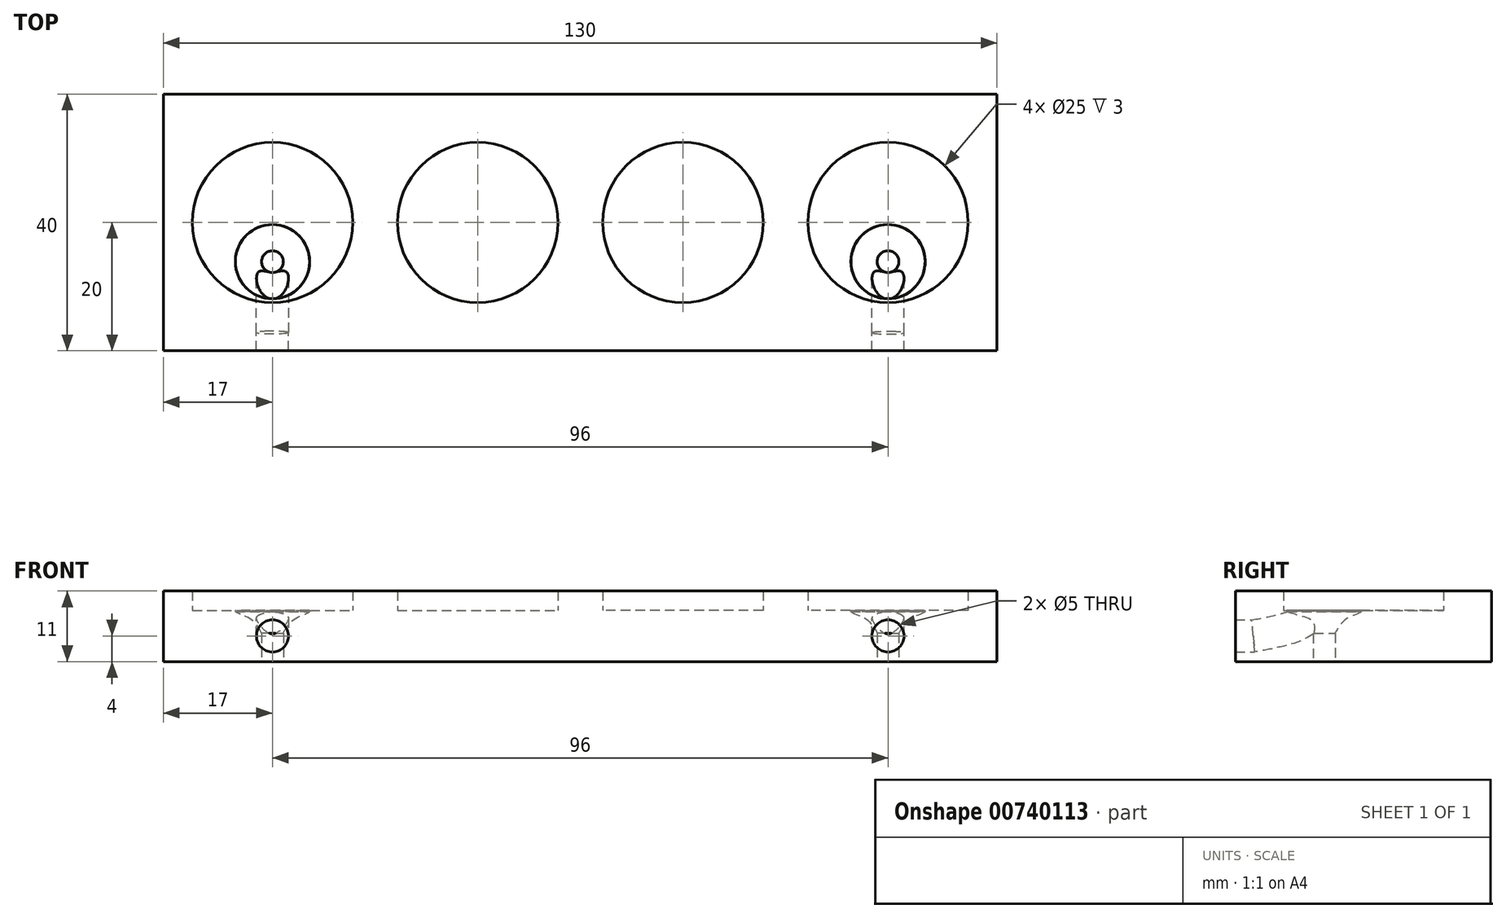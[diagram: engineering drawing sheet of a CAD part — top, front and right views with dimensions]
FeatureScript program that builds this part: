
annotation { "Feature Type Name" : "Feature", "Feature Type Description" : "" }
export const myFeature = defineFeature(function(context is Context, id is Id, definition is map)
    precondition{}
    {
        {
            var Q0;
            Q0=qCreatedBy(makeId("Top.planeOp"),FACE);
            var sketch = newSketch(context, id + "F0", { "sketchPlane" : qUnion([Q0])});
            skLineSegment(sketch, "E0.bottom", {"start": v(65, 20) * mm, "end": v(-65, 20) * mm});
            skLineSegment(sketch, "E0.top", {"start": v(65, -20) * mm, "end": v(-65, -20) * mm});
            skLineSegment(sketch, "E0.left", {"start": v(65, 20) * mm, "end": v(65, -20) * mm});
            skLineSegment(sketch, "E0.right", {"start": v(-65, 20) * mm, "end": v(-65, -20) * mm});
            skPoint(sketch, "E0.middle", {"position": v(0, 0) * mm});
            skCircle(sketch, "E1", {"center": v(-16, 0) * mm, "radius": 12.5 * mm});
            skCircle(sketch, "E2", {"center": v(-48, 0) * mm, "radius": 12.5 * mm});
            skCircle(sketch, "E3.MirrorC", {"center": v(16, 0) * mm, "radius": 12.5 * mm});
            skCircle(sketch, "E4.MirrorC", {"center": v(48, 0) * mm, "radius": 12.5 * mm});
            skSolve(sketch);
        }
        {
            var Q0;
            Q0=makeQuery(id+"F0.imprint","IMPRINT",FACE,{"disambiguationData":[TD([[makeQuery(id+"F0.imprint","IMPRINT",EDGE,{"derivedFrom":sQuery(id+"F0.wireOp",EDGE,"E0.bottom")}),1.0]])]});
            extrude(context, id + "F1", {"entities" : qUnion([Q0]), "depth" : 3 * mm, "offsetDistance" : 25.4 * mm});
        }
        {
            var Q0;
            Q0=qCreatedBy(makeId("Top.planeOp"),FACE);
            var sketch = newSketch(context, id + "F2", { "sketchPlane" : qUnion([Q0])});
            skLineSegment(sketch, "E5.bottom", {"start": v(65, -20) * mm, "end": v(-65, -20) * mm});
            skLineSegment(sketch, "E5.top", {"start": v(65, 20) * mm, "end": v(-65, 20) * mm});
            skLineSegment(sketch, "E5.left", {"start": v(65, -20) * mm, "end": v(65, 20) * mm});
            skLineSegment(sketch, "E5.right", {"start": v(-65, -20) * mm, "end": v(-65, 20) * mm});
            skPoint(sketch, "E5.middle", {"position": v(0, 0) * mm});
            skSolve(sketch);
        }
        {
            var Q0;
            Q0 = qSketchRegion(id + "F2", true);
            extrude(context, id + "F3", {"entities" : qUnion([Q0]), "operationType" : NewBodyOperationType.ADD, "oppositeDirection" : true, "depth" : 8 * mm, "offsetDistance" : 25.4 * mm});
        }
        {
            var Q0;
            Q0=qCreatedBy(makeId("Front.planeOp"),FACE);
            var sketch = newSketch(context, id + "F4", { "sketchPlane" : qUnion([Q0])});
            skLineSegment(sketch, "E6", {"start": v(60.5, 0) * mm, "end": v(35.5, 0) * mm});
            skSolve(sketch);
        }
        {
            var Q0;
            Q0=qCreatedBy(makeId("Right.planeOp"),FACE);
            var sketch = newSketch(context, id + "F5", { "sketchPlane" : qUnion([Q0])});
            skLineSegment(sketch, "E7.bottom", {"start": v(35.81, -28.05) * mm, "end": v(-42.11, -28.05) * mm});
            skLineSegment(sketch, "E7.top", {"start": v(35.81, 17.28) * mm, "end": v(-42.11, 17.28) * mm});
            skLineSegment(sketch, "E7.left", {"start": v(35.81, -28.05) * mm, "end": v(35.81, 17.28) * mm});
            skLineSegment(sketch, "E7.right", {"start": v(-42.11, -28.05) * mm, "end": v(-42.11, 17.28) * mm});
            skSolve(sketch);
        }
        {
            var Q0;
            Q0=makeQuery(id+"F5.imprint","IMPRINT",FACE,{"disambiguationData":[TD([[makeQuery(id+"F5.imprint","IMPRINT",EDGE,{"derivedFrom":sQuery(id+"F5.wireOp",EDGE,"E7.bottom")}),-1.0]])]});
            extrude(context, id + "F6", {"entities" : qUnion([Q0]), "operationType" : NewBodyOperationType.REMOVE, "oppositeDirection" : true, "depth" : 83 * mm, "offsetDistance" : 25 * mm});
        }
        {
            var Q0;
            Q0=sQuery(id+"F4.wireOp",EDGE,"E6");
            cPoint(context, id + "F7", {"entities" : qUnion([Q0]), "parameter" : 0.5});
        }
        {
            var Q0;
            Q0 = qCreatedBy(id + "F7" ,VERTEX);
            var Q1;
            Q1=qCreatedBy(makeId("Right.planeOp"),FACE);
            cPlane(context, id + "F8", {"entities" : qUnion([Q0, Q1]), "cplaneType" : CPlaneType.PLANE_POINT, "offset" : 25 * mm, "width" : 150 * mm, "height" : 150 * mm});
        }
        {
            var Q0;
            Q0=qCreatedBy(id+"F8.planeOp",FACE);
            var sketch = newSketch(context, id + "F9", { "sketchPlane" : qUnion([Q0])});
            skLineSegment(sketch, "E8", {"start": v(0, 0) * mm, "end": v(-20, 0) * mm, "construction": true});
            skLineSegment(sketch, "E9", {"start": v(0, 2.56) * mm, "end": v(-13, 2.56) * mm, "construction": true});
            skLineSegment(sketch, "E10", {"start": v(0, 0) * mm, "end": v(0, -8) * mm, "construction": true});
            skLineSegment(sketch, "E11", {"start": v(0, -4) * mm, "end": v(-14.4, -4) * mm, "construction": true});
            skLineSegment(sketch, "E12", {"start": v(-20, -4) * mm, "end": v(-17.2, -4) * mm});
            skLineSegment(sketch, "E13", {"start": v(-6.5, 2.56) * mm, "end": v(-6.5, -9.38) * mm, "construction": true});
            skLineSegment(sketch, "E14.trimOffspring", {"start": v(-17.2, -4) * mm, "end": v(-28.78, -4) * mm, "construction": true});
            skFitSpline(sketch, "E15", {"points": [v(-6.5, 2.56) * mm, v(-6.72, 1.46) * mm, v(-7.26, 0.3) * mm, v(-8.77, -1.28) * mm, v(-11.18, -2.61) * mm, v(-17.2, -4) * mm], "startDerivative": vector(-1.35, -8.2) * mm, "endDerivative": vector(-21.14, -3.95) * mm});
            skSolve(sketch);
        }
        {
            var Q0;
            Q0=makeQuery(id+"F3.boolean.opBoolean","MERGE",FACE,{"derivedFrom":[makeQuery(id+"F1.opExtrude","SWEPT_FACE",FACE,{"disambiguationData":[OSD([sQuery(id+"F0.wireOp",EDGE,"E0.top")])]}),makeQuery(id+"F3.opExtrude","SWEPT_FACE",FACE,{"disambiguationData":[OSD([sQuery(id+"F2.wireOp",EDGE,"E5.bottom")])]})]});
            var sketch = newSketch(context, id + "F10", { "sketchPlane" : qUnion([Q0])});
            skPoint(sketch, "E16.0", {"position": v(48, -4) * mm});
            skCircle(sketch, "E17", {"center": v(48, -4) * mm, "radius": 2.5 * mm});
            skSolve(sketch);
        }
        {
            var Q0;
            Q0=makeQuery(id+"F10.imprint","IMPRINT",FACE,{"disambiguationData":[TD([[makeQuery(id+"F10.imprint","IMPRINT",EDGE,{"derivedFrom":sQuery(id+"F10.wireOp",EDGE,"E17")}),1.0]])]});
            var Q1;
            Q1=sQuery(id+"F9.wireOp",EDGE,"E12");
            var Q2;
            Q2=sQuery(id+"F9.wireOp",EDGE,"E15");
            sweep(context, id + "F11", {"operationType" : NewBodyOperationType.REMOVE, "profiles" : qUnion([Q0]), "path" : qUnion([Q1, Q2])});
        }
        {
            var Q0;
            Q0=makeQuery(id+"F3.boolean.opBoolean","SPLIT",FACE,{"disambiguationData":[TD([makeQuery(id+"F1.opExtrude","SWEPT_FACE",FACE,{"disambiguationData":[OSD([sQuery(id+"F0.wireOp",EDGE,"E4.MirrorC")])]})])],"derivedFrom":makeQuery(id+"F3.opExtrude","CAP_FACE",FACE,{"disambiguationData":[OSD([sQuery(id+"F2.wireOp",EDGE,"E5.bottom"),sQuery(id+"F2.wireOp",EDGE,"E5.top"),sQuery(id+"F2.wireOp",EDGE,"E5.left"),sQuery(id+"F2.wireOp",EDGE,"E5.right")])],"isStart":true})});
            var sketch = newSketch(context, id + "F12", { "sketchPlane" : qUnion([Q0])});
            skLineSegment(sketch, "E18", {"start": v(48, -12.5) * mm, "end": v(48, 13) * mm, "construction": true});
            skLineSegment(sketch, "E19", {"start": v(48, 0.25) * mm, "end": v(48, -12.5) * mm, "construction": true});
            skSolve(sketch);
        }
        {
            var Q0;
            Q0=qCreatedBy(id+"F8.planeOp",FACE);
            var sketch = newSketch(context, id + "F13", { "sketchPlane" : qUnion([Q0])});
            skPoint(sketch, "E20.0", {"position": v(-6.12, 0) * mm});
            skFitSpline(sketch, "E21.0", {"points": [v(-11.4, 0) * mm, v(-9.13, 0) * mm, v(-6.86, 0) * mm, v(-4.6, 0) * mm]});
            skLineSegment(sketch, "E22", {"start": v(-6.32, -9.5) * mm, "end": v(-7.82, -9.5) * mm});
            skFitSpline(sketch, "E23", {"points": [v(-11.92, 0) * mm, v(-11.92, -0.17) * mm, v(-11.92, -0.23) * mm, v(-10.57, -0.84) * mm, v(-9.28, -1.55) * mm, v(-8.24, -2.83) * mm, v(-7.82, -3.56) * mm, v(-7.82, -3.6) * mm], "startDerivative": vector(0.18, -2.66) * mm, "endDerivative": vector(-0.17, -1.01) * mm});
            skLineSegment(sketch, "E24", {"start": v(-7.82, -3.58) * mm, "end": v(-7.82, -9.5) * mm});
            skLineSegment(sketch, "E25", {"start": v(-11.92, 0) * mm, "end": v(-6.12, 0) * mm});
            skLineSegment(sketch, "E26", {"start": v(-11.92, 0) * mm, "end": v(-11.91, -0.23) * mm});
            skFitSpline(sketch, "E27", {"points": [v(-7.82, -3.58) * mm, v(-8.03, -2.35) * mm, v(-9.14, -1.15) * mm, v(-11.91, -0.23) * mm], "startDerivative": vector(-0.23, 4.62) * mm, "endDerivative": vector(-7.37, 1.76) * mm});
            skLineSegment(sketch, "E28", {"start": v(-6.12, 0) * mm, "end": v(-6.12, -9.5) * mm});
            skLineSegment(sketch, "E29", {"start": v(-6.12, -9.5) * mm, "end": v(-6.32, -9.5) * mm});
            skSolve(sketch);
        }
        {
            var Q0;
            Q0 = qSketchRegion(id + "F13", true);
            var Q1;
            Q1=sQuery(id+"F13.wireOp",EDGE,"E28");
            revolve(context, id + "F14", {"operationType" : NewBodyOperationType.REMOVE, "surfaceOperationType" : NewSurfaceOperationType.NEW, "entities" : qUnion([Q0]), "axis" : qUnion([Q1]), "revolveType" : RevolveType.FULL, "oppositeDirection" : true});
        }
        {
            var Q0;
            Q0=qCreatedBy(makeId("Top.planeOp"),FACE);
            var sketch = newSketch(context, id + "F15", { "sketchPlane" : qUnion([Q0])});
            skPoint(sketch, "E30.0", {"position": v(48, 0.25) * mm});
            skLineSegment(sketch, "E31.0.0", {"start": v(0, 20) * mm, "end": v(0, -20) * mm});
            skLineSegment(sketch, "E31.0.1", {"start": v(0, -20) * mm, "end": v(65, -20) * mm});
            skLineSegment(sketch, "E31.0.2", {"start": v(65, -20) * mm, "end": v(65, 20) * mm});
            skLineSegment(sketch, "E31.0.3", {"start": v(65, 20) * mm, "end": v(0, 20) * mm});
            skCircle(sketch, "E32", {"center": v(16, 0) * mm, "radius": 12.5 * mm});
            skLineSegment(sketch, "E33", {"start": v(48, 0.25) * mm, "end": v(16, 0) * mm, "construction": true});
            skCircle(sketch, "E34", {"center": v(16, 0) * mm, "radius": 12.5 * mm, "construction": true});
            skCircle(sketch, "E35", {"center": v(48, 0) * mm, "radius": 12.5 * mm, "construction": true});
            skFitSpline(sketch, "E36", {"points": [v(50.3, -7.48) * mm, v(50.3, -7.28) * mm, v(50.28, -6.99) * mm, v(50.2, -6.6) * mm, v(50.09, -6.22) * mm, v(49.88, -5.78) * mm, v(49.57, -5.38) * mm, v(49.28, -5.12) * mm, v(49.04, -4.94) * mm, v(48.77, -4.8) * mm, v(48.4, -4.66) * mm, v(48, -4.59) * mm, v(47.62, -4.6) * mm, v(47.22, -4.65) * mm, v(46.85, -4.78) * mm, v(46.5, -4.98) * mm, v(46.19, -5.22) * mm, v(45.91, -5.52) * mm, v(45.7, -5.85) * mm, v(45.52, -6.2) * mm, v(45.37, -6.68) * mm, v(45.3, -7.27) * mm, v(45.3, -7.86) * mm, v(45.36, -8.25) * mm, v(45.4, -8.45) * mm, v(45.46, -8.69) * mm, v(45.6, -9.16) * mm, v(45.85, -9.72) * mm, v(46.11, -10.14) * mm, v(46.33, -10.44) * mm, v(46.57, -10.72) * mm, v(46.74, -10.9) * mm, v(46.84, -10.98) * mm, v(46.98, -11.1) * mm, v(47.2, -11.25) * mm, v(47.53, -11.37) * mm, v(47.8, -11.4) * mm, v(48.07, -11.37) * mm, v(48.4, -11.25) * mm, v(48.62, -11.1) * mm, v(48.76, -10.98) * mm, v(48.95, -10.82) * mm, v(49.2, -10.54) * mm, v(49.49, -10.14) * mm, v(49.75, -9.72) * mm, v(50, -9.16) * mm, v(50.14, -8.69) * mm, v(50.2, -8.45) * mm, v(50.26, -8.13) * mm, v(50.3, -7.8) * mm, v(50.3, -7.48) * mm], "construction": true});
            skSolve(sketch);
        }
        {
            var Q0;
            Q0=sQuery(id+"F15.wireOp",EDGE,"E33");
            cPoint(context, id + "F16", {"entities" : qUnion([Q0]), "parameter" : 0.5});
        }
        {
            var Q0;
            Q0 = qCreatedBy(id + "F16" ,VERTEX);
            var Q1;
            Q1=qCreatedBy(makeId("Right.planeOp"),FACE);
            cPlane(context, id + "F17", {"entities" : qUnion([Q0, Q1]), "cplaneType" : CPlaneType.PLANE_POINT, "offset" : 25 * mm, "width" : 150 * mm, "height" : 150 * mm});
        }
        {
            var Q0;
            Q0=makeQuery(id+"F1.opExtrude","SWEPT_BODY",BODY,{"disambiguationData":[OSD([sQuery(id+"F0.wireOp",EDGE,"E0.bottom"),sQuery(id+"F0.wireOp",EDGE,"E0.top"),sQuery(id+"F0.wireOp",EDGE,"E0.left"),sQuery(id+"F0.wireOp",EDGE,"E0.right"),sQuery(id+"F0.wireOp",EDGE,"E1"),sQuery(id+"F0.wireOp",EDGE,"E2"),sQuery(id+"F0.wireOp",EDGE,"E3.MirrorC"),sQuery(id+"F0.wireOp",EDGE,"E4.MirrorC")])]});
            var Q1;
            Q1=qCreatedBy(makeId("Right.planeOp"),FACE);
            mirror(context, id + "F18", {"operationType" : NewBodyOperationType.ADD, "entities" : qUnion([Q0]), "mirrorPlane" : qUnion([Q1])});
        }
    });
